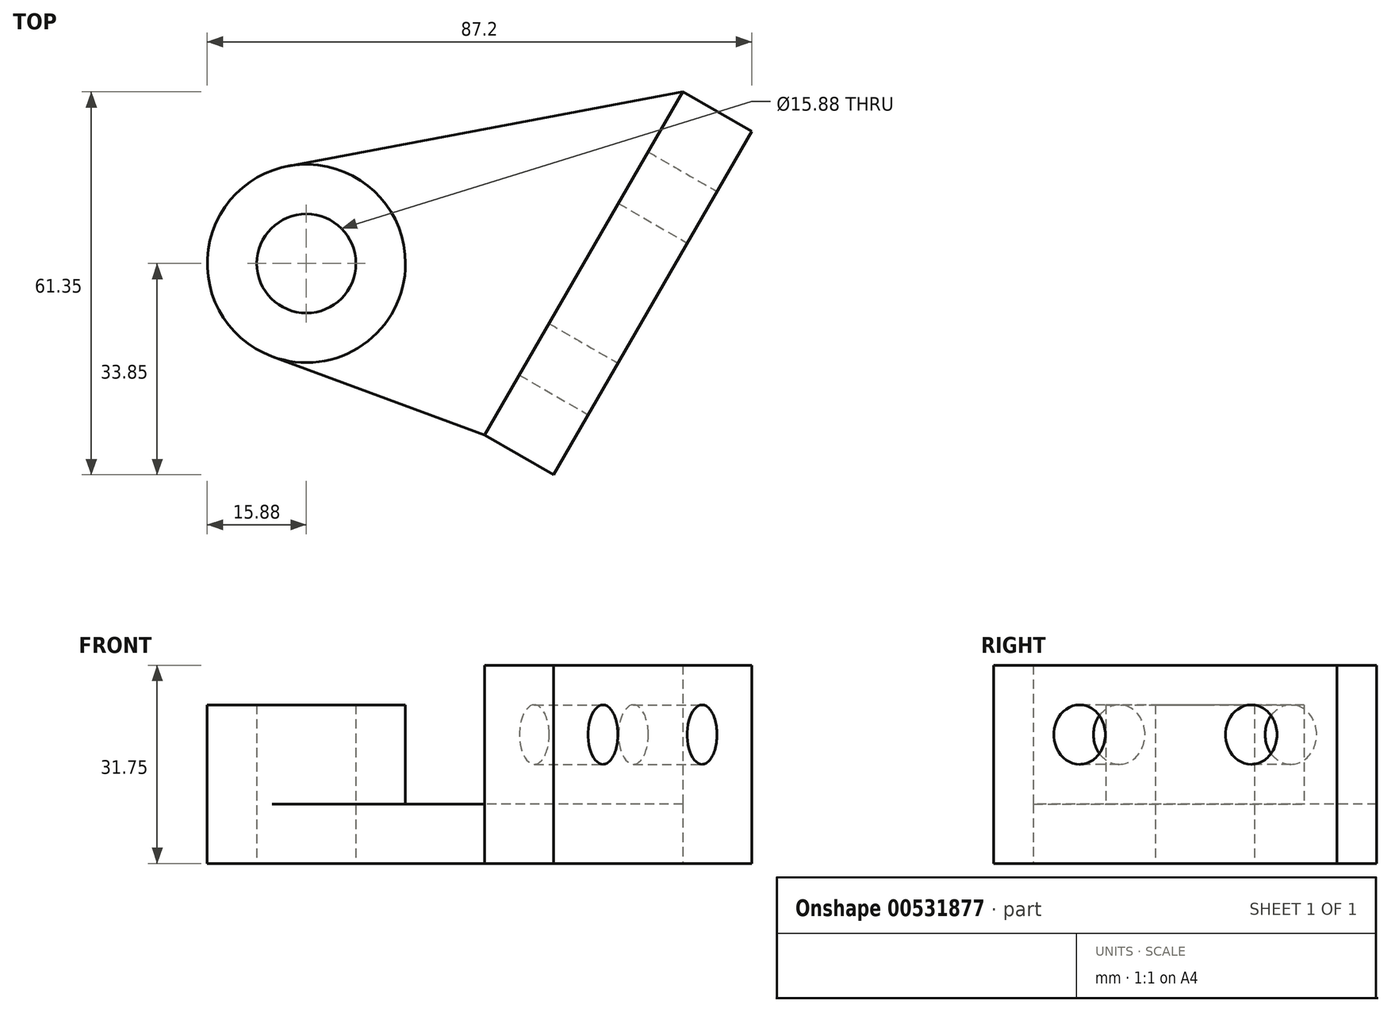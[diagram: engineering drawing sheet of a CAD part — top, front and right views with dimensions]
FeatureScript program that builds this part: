
annotation { "Feature Type Name" : "Feature", "Feature Type Description" : "" }
export const myFeature = defineFeature(function(context is Context, id is Id, definition is map)
    precondition{}
    {
        {
            var Q0;
            Q0=qCreatedBy(makeId("Top.planeOp"),FACE);
            var sketch = newSketch(context, id + "F0", { "sketchPlane" : qUnion([Q0])});
            skCircle(sketch, "E0", {"center": v(0, 0) * mm, "radius": 15.88 * mm});
            skCircle(sketch, "E1", {"center": v(0, 0) * mm, "radius": 7.94 * mm});
            skLineSegment(sketch, "E2", {"start": v(-37.63, 0) * mm, "end": v(71.51, 0) * mm, "construction": true});
            skLineSegment(sketch, "E3", {"start": v(44.45, 47.68) * mm, "end": v(44.45, -47.68) * mm, "construction": true});
            skPoint(sketch, "E4", {"position": v(44.45, 0) * mm});
            skLineSegment(sketch, "E5", {"start": v(60.33, 27.5) * mm, "end": v(28.58, -27.5) * mm});
            skLineSegment(sketch, "E6.0", {"start": v(71.32, 21.15) * mm, "end": v(39.57, -33.85) * mm});
            skLineSegment(sketch, "E7", {"start": v(28.58, -27.5) * mm, "end": v(39.57, -33.85) * mm});
            skLineSegment(sketch, "E8", {"start": v(60.33, 27.5) * mm, "end": v(71.32, 21.15) * mm});
            skLineSegment(sketch, "E9", {"start": v(60.33, 27.5) * mm, "end": v(-2.93, 15.6) * mm});
            skLineSegment(sketch, "E10", {"start": v(28.58, -27.5) * mm, "end": v(-5.5, -14.89) * mm});
            skSolve(sketch);
        }
        {
            var Q0;
            Q0=makeQuery(id+"F0.imprint","IMPRINT",FACE,{"disambiguationData":[TD([[makeQuery(id+"F0.imprint","IMPRINT",EDGE,{"derivedFrom":sQuery(id+"F0.wireOp",EDGE,"E5")}),-1.0]])]});
            extrude(context, id + "F1", {"entities" : qUnion([Q0]), "depth" : 9.52 * mm, "offsetDistance" : 25.4 * mm});
        }
        {
            var Q0;
            Q0=makeQuery(id+"F0.imprint","IMPRINT",FACE,{"disambiguationData":[TD([[makeQuery(id+"F0.imprint","IMPRINT",EDGE,{"derivedFrom":sQuery(id+"F0.wireOp",EDGE,"E1")}),-1.0]])]});
            extrude(context, id + "F2", {"entities" : qUnion([Q0]), "operationType" : NewBodyOperationType.ADD, "depth" : 25.4 * mm, "offsetDistance" : 25.4 * mm});
        }
        {
            var Q0;
            Q0=makeQuery(id+"F0.imprint","IMPRINT",FACE,{"disambiguationData":[TD([[makeQuery(id+"F0.imprint","IMPRINT",EDGE,{"derivedFrom":sQuery(id+"F0.wireOp",EDGE,"E5")}),1.0]])]});
            extrude(context, id + "F3", {"entities" : qUnion([Q0]), "operationType" : NewBodyOperationType.ADD, "depth" : 31.75 * mm, "offsetDistance" : 25.4 * mm});
        }
        {
            var Q0;
            Q0=makeQuery(id+"F3.opExtrude","SWEPT_FACE",FACE,{"disambiguationData":[OSD([sQuery(id+"F0.wireOp",EDGE,"E6.0")])]});
            var sketch = newSketch(context, id + "F4", { "sketchPlane" : qUnion([Q0])});
            skCircle(sketch, "E11", {"center": v(6.35, 20.64) * mm, "radius": 4.76 * mm});
            skCircle(sketch, "E12", {"center": v(38.1, 20.64) * mm, "radius": 4.76 * mm});
            skSolve(sketch);
        }
        {
            var Q0;
            Q0=makeQuery(id+"F4.imprint","IMPRINT",FACE,{"disambiguationData":[TD([[makeQuery(id+"F4.imprint","IMPRINT",EDGE,{"derivedFrom":sQuery(id+"F4.wireOp",EDGE,"E11")}),1.0]])]});
            var Q1;
            Q1=makeQuery(id+"F4.imprint","IMPRINT",FACE,{"disambiguationData":[TD([[makeQuery(id+"F4.imprint","IMPRINT",EDGE,{"derivedFrom":sQuery(id+"F4.wireOp",EDGE,"E12")}),1.0]])]});
            extrude(context, id + "F5", {"entities" : qUnion([Q0, Q1]), "operationType" : NewBodyOperationType.REMOVE, "endBound" : BoundingType.UP_TO_NEXT, "oppositeDirection" : true, "depth" : 25.4 * mm, "offsetDistance" : 25.4 * mm});
        }
    });
